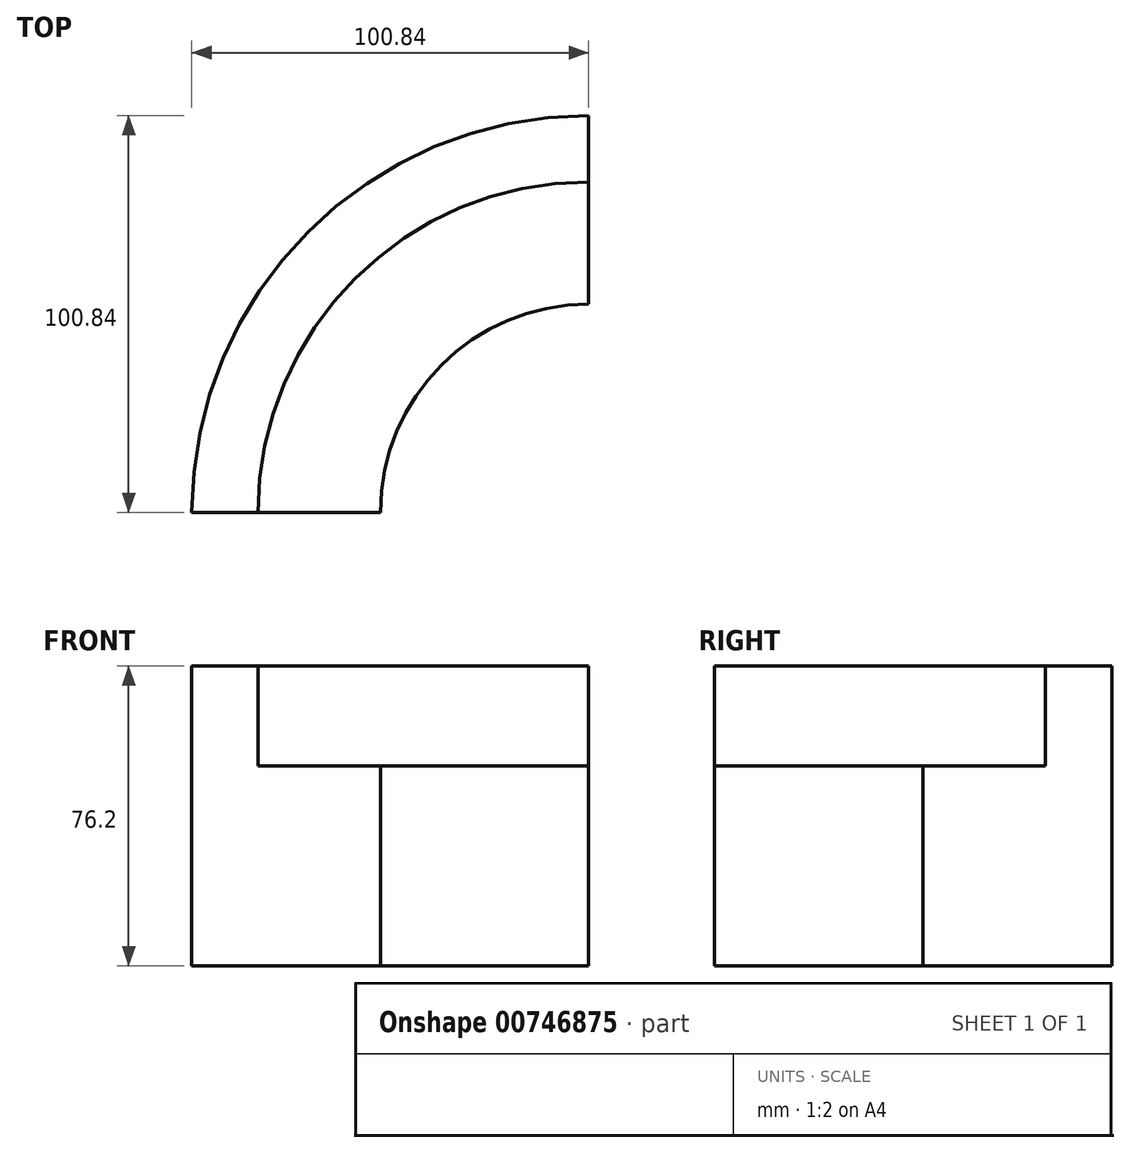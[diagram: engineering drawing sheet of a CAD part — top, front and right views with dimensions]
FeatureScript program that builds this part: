
annotation { "Feature Type Name" : "Feature", "Feature Type Description" : "" }
export const myFeature = defineFeature(function(context is Context, id is Id, definition is map)
    precondition{}
    {
        {
            var Q0;
            Q0=qCreatedBy(makeId("Top.planeOp"),FACE);
            var sketch = newSketch(context, id + "F0", { "sketchPlane" : qUnion([Q0])});
            skCircle(sketch, "E0", {"center": v(0, 0) * mm, "radius": 100.84 * mm});
            skLineSegment(sketch, "E1", {"start": v(0, 0) * mm, "end": v(0, 100.84) * mm});
            skLineSegment(sketch, "E2", {"start": v(0, 0) * mm, "end": v(-100.84, 0) * mm});
            skCircle(sketch, "E3", {"center": v(0, 0) * mm, "radius": 84 * mm});
            skCircle(sketch, "E4", {"center": v(0, 0) * mm, "radius": 52.94 * mm});
            skSolve(sketch);
        }
        {
            var Q0;
            {var subQ0=sQuery(id+"F0.wireOp",EDGE,"E1");var subQ1=sQuery(id+"F0.wireOp",EDGE,"E0");var subQ2=makeQuery(id+"F0.imprint","INTERSECT",VERTEX,{"derivedFrom":[subQ1,subQ0]});Q0=makeQuery(id+"F0.imprint","IMPRINT",FACE,{"disambiguationData":[TD([[makeQuery(id+"F0.imprint","IMPRINT",EDGE,{"disambiguationData":[TD([[subQ2,-1.0]])],"derivedFrom":subQ1}),1.0]])]});}
            extrude(context, id + "F1", {"entities" : qUnion([Q0]), "depth" : 76.2 * mm, "offsetDistance" : 25.4 * mm});
        }
        {
            var Q0;
            {var subQ0=sQuery(id+"F0.wireOp",EDGE,"E4");var subQ1=sQuery(id+"F0.wireOp",EDGE,"E1");var subQ2=makeQuery(id+"F0.imprint","INTERSECT",VERTEX,{"derivedFrom":[subQ1,subQ0]});Q0=makeQuery(id+"F0.imprint","IMPRINT",FACE,{"disambiguationData":[TD([[makeQuery(id+"F0.imprint","IMPRINT",EDGE,{"disambiguationData":[TD([[subQ2,-1.0]])],"derivedFrom":subQ1}),1.0]])]});}
            extrude(context, id + "F2", {"entities" : qUnion([Q0]), "operationType" : NewBodyOperationType.ADD, "depth" : 50.8 * mm, "offsetDistance" : 25.4 * mm});
        }
    });
